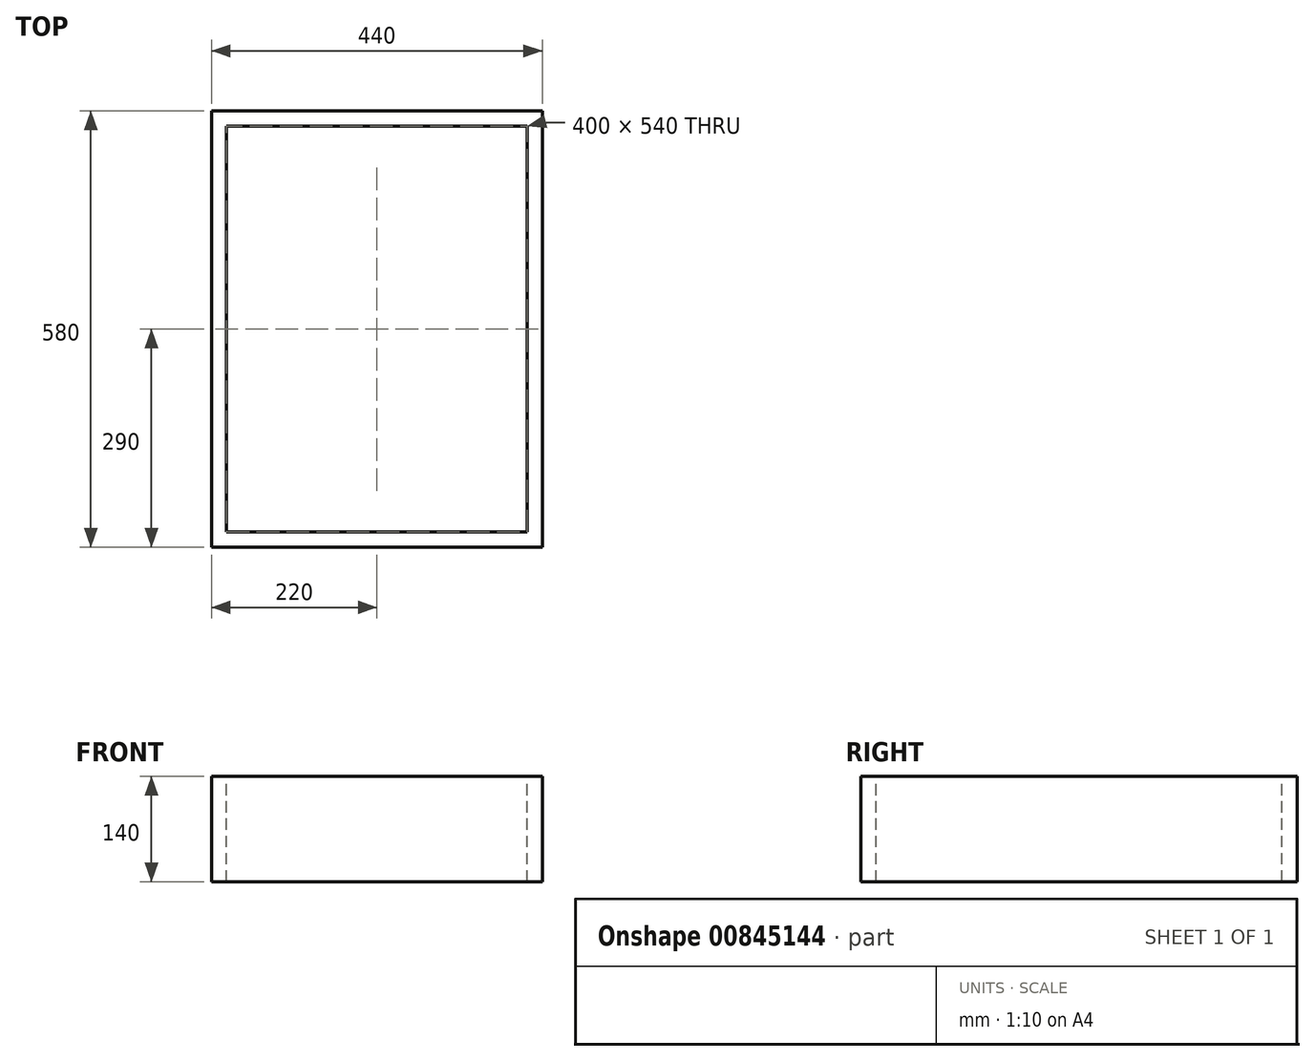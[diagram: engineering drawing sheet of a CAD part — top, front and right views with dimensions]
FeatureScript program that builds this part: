
annotation { "Feature Type Name" : "Feature", "Feature Type Description" : "" }
export const myFeature = defineFeature(function(context is Context, id is Id, definition is map)
    precondition{}
    {
        {
            var Q0;
            Q0=qCreatedBy(makeId("Top.planeOp"),FACE);
            var sketch = newSketch(context, id + "F0", { "sketchPlane" : qUnion([Q0])});
            skLineSegment(sketch, "E0.bottom", {"start": v(0, 0) * mm, "end": v(440, 0) * mm});
            skLineSegment(sketch, "E0.top", {"start": v(0, 580) * mm, "end": v(440, 580) * mm});
            skLineSegment(sketch, "E0.left", {"start": v(0, 0) * mm, "end": v(0, 580) * mm});
            skLineSegment(sketch, "E0.right", {"start": v(440, 0) * mm, "end": v(440, 580) * mm});
            skSolve(sketch);
        }
        {
            var Q0;
            Q0=makeQuery(id+"F0.imprint","IMPRINT",FACE,{"disambiguationData":[TD([[makeQuery(id+"F0.imprint","IMPRINT",EDGE,{"derivedFrom":sQuery(id+"F0.wireOp",EDGE,"E0.bottom")}),1.0]])]});
            extrude(context, id + "F1", {"entities" : qUnion([Q0]), "depth" : 140 * mm, "offsetDistance" : 25 * mm});
        }
        {
            var Q0;
            Q0=makeQuery(id+"F1.opExtrude","CAP_FACE",FACE,{"disambiguationData":[OSD([sQuery(id+"F0.wireOp",EDGE,"E0.bottom"),sQuery(id+"F0.wireOp",EDGE,"E0.top"),sQuery(id+"F0.wireOp",EDGE,"E0.left"),sQuery(id+"F0.wireOp",EDGE,"E0.right")])],"isStart":false});
            var sketch = newSketch(context, id + "F2", { "sketchPlane" : qUnion([Q0])});
            skLineSegment(sketch, "E1.bottom", {"start": v(20, 20) * mm, "end": v(420, 20) * mm});
            skLineSegment(sketch, "E1.top", {"start": v(20, 560) * mm, "end": v(420, 560) * mm});
            skLineSegment(sketch, "E1.left", {"start": v(20, 20) * mm, "end": v(20, 560) * mm});
            skLineSegment(sketch, "E1.right", {"start": v(420, 20) * mm, "end": v(420, 560) * mm});
            skSolve(sketch);
        }
        {
            var Q0;
            Q0=makeQuery(id+"F2.imprint","IMPRINT",FACE,{"disambiguationData":[TD([[makeQuery(id+"F2.imprint","IMPRINT",EDGE,{"derivedFrom":sQuery(id+"F2.wireOp",EDGE,"E1.bottom")}),1.0]])]});
            var Q1;
            Q1=makeQuery(id+"F1.opExtrude","CAP_FACE",FACE,{"disambiguationData":[OSD([sQuery(id+"F0.wireOp",EDGE,"E0.bottom"),sQuery(id+"F0.wireOp",EDGE,"E0.top"),sQuery(id+"F0.wireOp",EDGE,"E0.left"),sQuery(id+"F0.wireOp",EDGE,"E0.right")])],"isStart":true});
            extrude(context, id + "F3", {"entities" : qUnion([Q0]), "operationType" : NewBodyOperationType.REMOVE, "endBound" : BoundingType.UP_TO_SURFACE, "oppositeDirection" : true, "depth" : 25 * mm, "endBoundEntityFace" : qUnion([Q1]), "offsetDistance" : 25 * mm});
        }
    });
